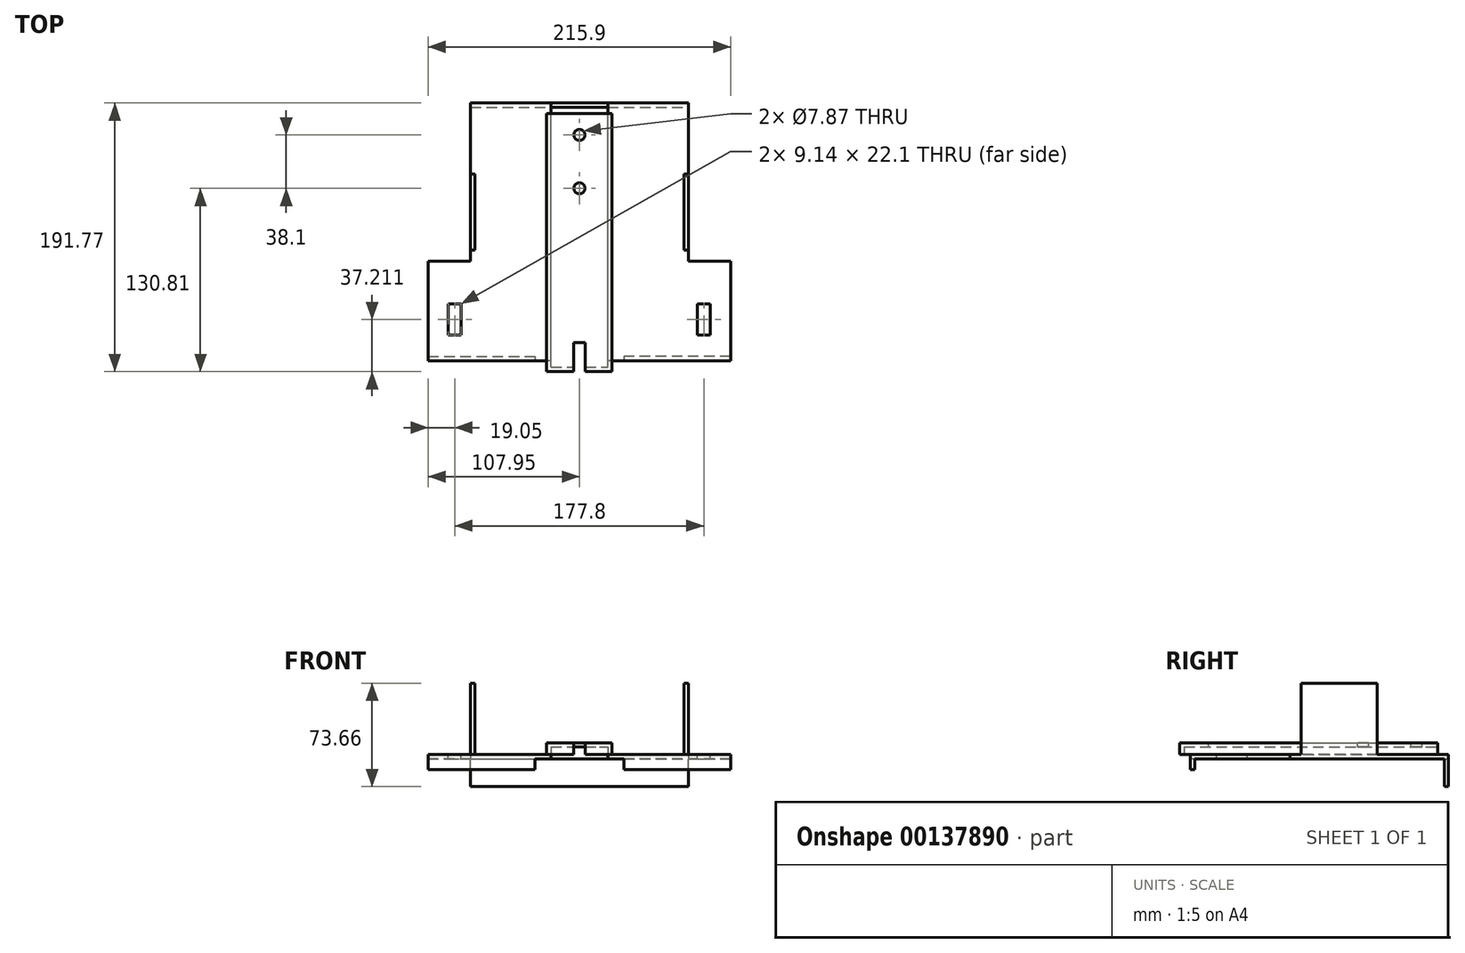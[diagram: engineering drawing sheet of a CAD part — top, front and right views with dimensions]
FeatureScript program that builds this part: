
annotation { "Feature Type Name" : "Feature", "Feature Type Description" : "" }
export const myFeature = defineFeature(function(context is Context, id is Id, definition is map)
    precondition{}
    {
        {
            var Q0;
            Q0=qCreatedBy(makeId("Top.planeOp"),FACE);
            var sketch = newSketch(context, id + "F0", { "sketchPlane" : qUnion([Q0])});
            skLineSegment(sketch, "E0.bottom", {"start": v(107.95, 0) * mm, "end": v(-107.95, 0) * mm});
            skLineSegment(sketch, "E0.top", {"start": v(77.79, 184.15) * mm, "end": v(-77.79, 184.15) * mm});
            skLineSegment(sketch, "E0.left", {"start": v(107.95, 0) * mm, "end": v(107.95, 71.12) * mm});
            skLineSegment(sketch, "E0.right", {"start": v(-107.95, 0) * mm, "end": v(-107.95, 71.12) * mm});
            skPoint(sketch, "E0.middle", {"position": v(0, 0) * mm});
            skLineSegment(sketch, "E1", {"start": v(-77.79, 184.15) * mm, "end": v(-77.79, 71.12) * mm});
            skLineSegment(sketch, "E2", {"start": v(-77.79, 71.12) * mm, "end": v(-107.95, 71.12) * mm});
            skLineSegment(sketch, "E3.MirrorCS", {"start": v(77.79, 184.15) * mm, "end": v(77.79, 71.12) * mm});
            skLineSegment(sketch, "E4.MirrorCS", {"start": v(77.79, 71.12) * mm, "end": v(107.95, 71.12) * mm});
            skLineSegment(sketch, "E5", {"start": v(0, 184.15) * mm, "end": v(0, 0) * mm, "construction": true});
            skSolve(sketch);
        }
        {
            var Q0;
            Q0 = qSketchRegion(id + "F0", true);
            extrude(context, id + "F1", {"entities" : qUnion([Q0]), "depth" : 3.1 * mm});
        }
        {
            var Q0;
            Q0=makeQuery(id+"F1.opExtrude","CAP_FACE",FACE,{"disambiguationData":[OSD([sQuery(id+"F0.wireOp",EDGE,"E0.bottom"),sQuery(id+"F0.wireOp",EDGE,"E0.top"),sQuery(id+"F0.wireOp",EDGE,"E0.left"),sQuery(id+"F0.wireOp",EDGE,"E0.right"),sQuery(id+"F0.wireOp",EDGE,"E1"),sQuery(id+"F0.wireOp",EDGE,"E2"),sQuery(id+"F0.wireOp",EDGE,"E3.MirrorCS"),sQuery(id+"F0.wireOp",EDGE,"E4.MirrorCS")])],"isStart":false});
            var sketch = newSketch(context, id + "F2", { "sketchPlane" : qUnion([Q0])});
            skLineSegment(sketch, "E6.bottom", {"start": v(107.95, 0) * mm, "end": v(31.75, 0) * mm});
            skLineSegment(sketch, "E6.top", {"start": v(107.95, 3.1) * mm, "end": v(31.75, 3.1) * mm});
            skLineSegment(sketch, "E6.left", {"start": v(107.95, 3.1) * mm, "end": v(107.95, 0) * mm});
            skLineSegment(sketch, "E6.right", {"start": v(31.75, 3.1) * mm, "end": v(31.75, 0) * mm});
            skLineSegment(sketch, "E7.MirrorCS", {"start": v(-31.75, 3.1) * mm, "end": v(-31.75, 0) * mm});
            skLineSegment(sketch, "E8.MirrorCS", {"start": v(-107.95, 3.1) * mm, "end": v(-107.95, 0) * mm});
            skLineSegment(sketch, "E9.MirrorCS", {"start": v(-107.95, 0) * mm, "end": v(-31.75, 0) * mm});
            skLineSegment(sketch, "E10.MirrorCS", {"start": v(-107.95, 3.1) * mm, "end": v(-31.75, 3.1) * mm});
            skSolve(sketch);
        }
        {
            var Q0;
            Q0 = qSketchRegion(id + "F2", true);
            extrude(context, id + "F3", {"entities" : qUnion([Q0]), "operationType" : NewBodyOperationType.ADD, "oppositeDirection" : true, "depth" : 10.92 * mm});
        }
        {
            var Q0;
            Q0=makeQuery(id+"F1.opExtrude","CAP_FACE",FACE,{"disambiguationData":[OSD([sQuery(id+"F0.wireOp",EDGE,"E0.bottom"),sQuery(id+"F0.wireOp",EDGE,"E0.top"),sQuery(id+"F0.wireOp",EDGE,"E0.left"),sQuery(id+"F0.wireOp",EDGE,"E0.right"),sQuery(id+"F0.wireOp",EDGE,"E1"),sQuery(id+"F0.wireOp",EDGE,"E2"),sQuery(id+"F0.wireOp",EDGE,"E3.MirrorCS"),sQuery(id+"F0.wireOp",EDGE,"E4.MirrorCS")])],"isStart":false});
            var sketch = newSketch(context, id + "F4", { "sketchPlane" : qUnion([Q0])});
            skLineSegment(sketch, "E11.bottom", {"start": v(-77.79, 184.15) * mm, "end": v(77.79, 184.15) * mm});
            skLineSegment(sketch, "E11.top", {"start": v(-77.79, 181.05) * mm, "end": v(77.79, 181.05) * mm});
            skLineSegment(sketch, "E11.left", {"start": v(-77.79, 184.15) * mm, "end": v(-77.79, 181.05) * mm});
            skLineSegment(sketch, "E11.right", {"start": v(77.79, 184.15) * mm, "end": v(77.79, 181.05) * mm});
            skSolve(sketch);
        }
        {
            var Q0;
            Q0 = qSketchRegion(id + "F4", true);
            extrude(context, id + "F5", {"entities" : qUnion([Q0]), "operationType" : NewBodyOperationType.ADD, "oppositeDirection" : true, "depth" : 22.86 * mm});
        }
        {
            var Q0;
            Q0=makeQuery(id+"F1.opExtrude","CAP_FACE",FACE,{"disambiguationData":[OSD([sQuery(id+"F0.wireOp",EDGE,"E0.bottom"),sQuery(id+"F0.wireOp",EDGE,"E0.top"),sQuery(id+"F0.wireOp",EDGE,"E0.left"),sQuery(id+"F0.wireOp",EDGE,"E0.right"),sQuery(id+"F0.wireOp",EDGE,"E1"),sQuery(id+"F0.wireOp",EDGE,"E2"),sQuery(id+"F0.wireOp",EDGE,"E3.MirrorCS"),sQuery(id+"F0.wireOp",EDGE,"E4.MirrorCS")])],"isStart":false});
            var sketch = newSketch(context, id + "F6", { "sketchPlane" : qUnion([Q0])});
            skLineSegment(sketch, "E12.bottom", {"start": v(-23.33, -7.62) * mm, "end": v(23.33, -7.62) * mm});
            skLineSegment(sketch, "E12.left", {"start": v(-23.33, -7.62) * mm, "end": v(-23.33, 176.53) * mm});
            skLineSegment(sketch, "E12.right", {"start": v(23.33, -7.62) * mm, "end": v(23.33, 176.53) * mm});
            skLineSegment(sketch, "E13", {"start": v(-23.33, 176.53) * mm, "end": v(23.33, 176.53) * mm});
            skSolve(sketch);
        }
        {
            var Q0;
            Q0 = qSketchRegion(id + "F6", true);
            extrude(context, id + "F7", {"entities" : qUnion([Q0]), "operationType" : NewBodyOperationType.ADD, "depth" : 8.33 * mm});
        }
        {
            var Q0;
            Q0=makeQuery(id+"F1.opExtrude","CAP_FACE",FACE,{"disambiguationData":[OSD([sQuery(id+"F0.wireOp",EDGE,"E0.bottom"),sQuery(id+"F0.wireOp",EDGE,"E0.top"),sQuery(id+"F0.wireOp",EDGE,"E0.left"),sQuery(id+"F0.wireOp",EDGE,"E0.right"),sQuery(id+"F0.wireOp",EDGE,"E1"),sQuery(id+"F0.wireOp",EDGE,"E2"),sQuery(id+"F0.wireOp",EDGE,"E3.MirrorCS"),sQuery(id+"F0.wireOp",EDGE,"E4.MirrorCS")])],"isStart":true});
            var sketch = newSketch(context, id + "F8", { "sketchPlane" : qUnion([Q0])});
            skLineSegment(sketch, "E14.bottom", {"start": v(-20.23, 15.8) * mm, "end": v(20.23, 15.8) * mm});
            skLineSegment(sketch, "E14.top", {"start": v(-20.23, -199.77) * mm, "end": v(20.23, -199.77) * mm});
            skLineSegment(sketch, "E14.left", {"start": v(-20.23, 15.8) * mm, "end": v(-20.23, -199.77) * mm});
            skLineSegment(sketch, "E14.right", {"start": v(20.23, 15.8) * mm, "end": v(20.23, -199.77) * mm});
            skSolve(sketch);
        }
        {
            var Q0;
            Q0 = qSketchRegion(id + "F8", true);
            extrude(context, id + "F9", {"entities" : qUnion([Q0]), "operationType" : NewBodyOperationType.REMOVE, "oppositeDirection" : true, "depth" : 3.1 * mm});
        }
        {
            var Q0;
            Q0=makeQuery(id+"F9.boolean.opBoolean","MERGE",FACE,{"derivedFrom":[makeQuery(id+"F7.opExtrude","CAP_FACE",FACE,{"disambiguationData":[OSD([sQuery(id+"F6.wireOp",EDGE,"E12.bottom"),sQuery(id+"F6.wireOp",EDGE,"E12.left"),sQuery(id+"F6.wireOp",EDGE,"E12.right"),sQuery(id+"F6.wireOp",EDGE,"E13")])],"isStart":true}),makeQuery(id+"F9.opExtrude","CAP_FACE",FACE,{"disambiguationData":[OSD([sQuery(id+"F8.wireOp",EDGE,"E14.bottom"),sQuery(id+"F8.wireOp",EDGE,"E14.top"),sQuery(id+"F8.wireOp",EDGE,"E14.left"),sQuery(id+"F8.wireOp",EDGE,"E14.right")])],"isStart":false})]});
            shell(context, id + "F10", {"entities" : qUnion([Q0]), "thickness" : 3.1 * mm});
        }
        {
            var Q0;
            Q0=makeQuery(id+"F10.opShell","OFFSET_FACE",FACE,{"disambiguationData":[OSD([sQuery(id+"F6.wireOp",EDGE,"E13")])]});
            extrude(context, id + "F11", {"entities" : qUnion([Q0]), "operationType" : NewBodyOperationType.REMOVE, "endBound" : BoundingType.UP_TO_NEXT, "oppositeDirection" : true, "depth" : 25.4 * mm});
        }
        {
            var Q0;
            Q0=makeQuery(id+"F7.opExtrude","CAP_FACE",FACE,{"disambiguationData":[OSD([sQuery(id+"F6.wireOp",EDGE,"E12.bottom"),sQuery(id+"F6.wireOp",EDGE,"E12.left"),sQuery(id+"F6.wireOp",EDGE,"E12.right"),sQuery(id+"F6.wireOp",EDGE,"E13")])],"isStart":false});
            var sketch = newSketch(context, id + "F12", { "sketchPlane" : qUnion([Q0])});
            skLineSegment(sketch, "E15.bottom", {"start": v(-4.23, -7.62) * mm, "end": v(4.23, -7.62) * mm});
            skLineSegment(sketch, "E15.top", {"start": v(-4.23, 12.95) * mm, "end": v(4.23, 12.95) * mm});
            skLineSegment(sketch, "E15.left", {"start": v(-4.23, -7.62) * mm, "end": v(-4.23, 12.95) * mm});
            skLineSegment(sketch, "E15.right", {"start": v(4.23, -7.62) * mm, "end": v(4.23, 12.95) * mm});
            skSolve(sketch);
        }
        {
            var Q0;
            Q0 = qSketchRegion(id + "F12", true);
            var Q1;
            Q1=makeQuery(id+"F9.boolean.opBoolean","MERGE",FACE,{"derivedFrom":[makeQuery(id+"F7.opExtrude","CAP_FACE",FACE,{"disambiguationData":[OSD([sQuery(id+"F6.wireOp",EDGE,"E12.bottom"),sQuery(id+"F6.wireOp",EDGE,"E12.left"),sQuery(id+"F6.wireOp",EDGE,"E12.right"),sQuery(id+"F6.wireOp",EDGE,"E13")])],"isStart":true}),makeQuery(id+"F9.opExtrude","CAP_FACE",FACE,{"disambiguationData":[OSD([sQuery(id+"F8.wireOp",EDGE,"E14.bottom"),sQuery(id+"F8.wireOp",EDGE,"E14.top"),sQuery(id+"F8.wireOp",EDGE,"E14.left"),sQuery(id+"F8.wireOp",EDGE,"E14.right")])],"isStart":false})]});
            extrude(context, id + "F13", {"entities" : qUnion([Q0]), "operationType" : NewBodyOperationType.REMOVE, "endBound" : BoundingType.UP_TO_SURFACE, "oppositeDirection" : true, "endBoundEntityFace" : qUnion([Q1]), "depth" : 25.4 * mm});
        }
        {
            var Q0;
            {var subQ0=sQuery(id+"F0.wireOp",EDGE,"E1");var subQ1=sQuery(id+"F0.wireOp",EDGE,"E2");var subQ2=sQuery(id+"F0.wireOp",EDGE,"E0.bottom");var subQ3=sQuery(id+"F0.wireOp",EDGE,"E0.top");var subQ4=sQuery(id+"F0.wireOp",EDGE,"E0.right");Q0=makeQuery(id+"F9.boolean.opBoolean","SPLIT",FACE,{"disambiguationData":[TD([makeQuery(id+"F1.opExtrude","SWEPT_FACE",FACE,{"disambiguationData":[OSD([subQ4])]})])],"derivedFrom":makeQuery(id+"F1.opExtrude","CAP_FACE",FACE,{"disambiguationData":[OSD([subQ2,subQ3,sQuery(id+"F0.wireOp",EDGE,"E0.left"),subQ4,subQ0,subQ1,sQuery(id+"F0.wireOp",EDGE,"E3.MirrorCS"),sQuery(id+"F0.wireOp",EDGE,"E4.MirrorCS")])],"isStart":false})});}
            var sketch = newSketch(context, id + "F14", { "sketchPlane" : qUnion([Q0])});
            skLineSegment(sketch, "E16.bottom", {"start": v(-77.79, 133.35) * mm, "end": v(-74.69, 133.35) * mm});
            skLineSegment(sketch, "E16.top", {"start": v(-77.79, 79) * mm, "end": v(-74.69, 79) * mm});
            skLineSegment(sketch, "E16.left", {"start": v(-77.79, 133.35) * mm, "end": v(-77.79, 79) * mm});
            skLineSegment(sketch, "E16.right", {"start": v(-74.69, 133.35) * mm, "end": v(-74.69, 79) * mm});
            skLineSegment(sketch, "E17.MirrorCS", {"start": v(74.69, 133.35) * mm, "end": v(74.69, 79) * mm});
            skLineSegment(sketch, "E18.MirrorCS", {"start": v(77.79, 133.35) * mm, "end": v(77.79, 79) * mm});
            skLineSegment(sketch, "E19.MirrorCS", {"start": v(77.79, 133.35) * mm, "end": v(74.69, 133.35) * mm});
            skLineSegment(sketch, "E20.MirrorCS", {"start": v(77.79, 79) * mm, "end": v(74.69, 79) * mm});
            skSolve(sketch);
        }
        {
            var Q0;
            Q0 = qSketchRegion(id + "F14", true);
            extrude(context, id + "F15", {"entities" : qUnion([Q0]), "operationType" : NewBodyOperationType.ADD, "depth" : 50.8 * mm});
        }
        {
            var Q0;
            {var subQ0=sQuery(id+"F0.wireOp",EDGE,"E4.MirrorCS");var subQ1=sQuery(id+"F0.wireOp",EDGE,"E0.bottom");var subQ2=sQuery(id+"F0.wireOp",EDGE,"E0.left");var subQ3=sQuery(id+"F0.wireOp",EDGE,"E0.top");var subQ4=sQuery(id+"F0.wireOp",EDGE,"E3.MirrorCS");Q0=makeQuery(id+"F9.boolean.opBoolean","SPLIT",FACE,{"disambiguationData":[TD([makeQuery(id+"F1.opExtrude","SWEPT_FACE",FACE,{"disambiguationData":[OSD([subQ2])]})])],"derivedFrom":makeQuery(id+"F1.opExtrude","CAP_FACE",FACE,{"disambiguationData":[OSD([subQ1,subQ3,subQ2,sQuery(id+"F0.wireOp",EDGE,"E0.right"),sQuery(id+"F0.wireOp",EDGE,"E1"),sQuery(id+"F0.wireOp",EDGE,"E2"),subQ4,subQ0])],"isStart":false})});}
            var sketch = newSketch(context, id + "F16", { "sketchPlane" : qUnion([Q0])});
            skLineSegment(sketch, "E21.bottom", {"start": v(93.47, 18.54) * mm, "end": v(84.33, 18.54) * mm});
            skLineSegment(sketch, "E21.top", {"start": v(93.47, 40.64) * mm, "end": v(84.33, 40.64) * mm});
            skLineSegment(sketch, "E21.left", {"start": v(93.47, 18.54) * mm, "end": v(93.47, 40.64) * mm});
            skLineSegment(sketch, "E21.right", {"start": v(84.33, 18.54) * mm, "end": v(84.33, 40.64) * mm});
            skLineSegment(sketch, "E22", {"start": v(88.9, 40.64) * mm, "end": v(88.9, 18.54) * mm, "construction": true});
            skArc(sketch, "E23", {"start": v(93.47, 36.07) * mm, "mid": v(88.9, 40.64) * mm, "end": v(84.33, 36.07) * mm, "construction": true});
            skArc(sketch, "E24", {"start": v(84.33, 23.11) * mm, "mid": v(88.9, 18.54) * mm, "end": v(93.47, 23.11) * mm, "construction": true});
            skArc(sketch, "E25.MirrorCS", {"start": v(93.47, 23.11) * mm, "mid": v(88.9, 18.54) * mm, "end": v(84.33, 23.11) * mm, "construction": true});
            skArc(sketch, "E26.MirrorCS", {"start": v(84.33, 36.07) * mm, "mid": v(88.9, 40.64) * mm, "end": v(93.47, 36.07) * mm, "construction": true});
            skLineSegment(sketch, "E27.MirrorCS", {"start": v(84.33, 18.54) * mm, "end": v(93.47, 18.54) * mm});
            skLineSegment(sketch, "E28.MirrorCS", {"start": v(84.33, 40.64) * mm, "end": v(93.47, 40.64) * mm});
            skLineSegment(sketch, "E29.MirrorCS", {"start": v(-84.33, 18.54) * mm, "end": v(-84.33, 40.64) * mm});
            skLineSegment(sketch, "E30.MirrorCS", {"start": v(-84.33, 18.54) * mm, "end": v(-93.47, 18.54) * mm});
            skLineSegment(sketch, "E31.MirrorCS", {"start": v(-84.33, 40.64) * mm, "end": v(-93.47, 40.64) * mm});
            skLineSegment(sketch, "E32.MirrorCS", {"start": v(-93.47, 18.54) * mm, "end": v(-93.47, 40.64) * mm});
            skArc(sketch, "E33.MirrorCS", {"start": v(-84.33, 36.07) * mm, "mid": v(-88.9, 40.64) * mm, "end": v(-93.47, 36.07) * mm, "construction": true});
            skArc(sketch, "E34.MirrorCS", {"start": v(-93.47, 23.11) * mm, "mid": v(-88.9, 18.54) * mm, "end": v(-84.33, 23.11) * mm, "construction": true});
            skLineSegment(sketch, "E35.MirrorCS", {"start": v(-93.47, 40.64) * mm, "end": v(-84.33, 40.64) * mm});
            skLineSegment(sketch, "E36.MirrorCS", {"start": v(-93.47, 18.54) * mm, "end": v(-84.33, 18.54) * mm});
            skLineSegment(sketch, "E37.MirrorCS", {"start": v(-88.9, 40.64) * mm, "end": v(-88.9, 18.54) * mm, "construction": true});
            skArc(sketch, "E38.MirrorCS", {"start": v(-84.33, 23.11) * mm, "mid": v(-88.9, 18.54) * mm, "end": v(-93.47, 23.11) * mm, "construction": true});
            skArc(sketch, "E39.MirrorCS", {"start": v(-93.47, 36.07) * mm, "mid": v(-88.9, 40.64) * mm, "end": v(-84.33, 36.07) * mm, "construction": true});
            skSolve(sketch);
        }
        {
            var Q0;
            Q0 = qSketchRegion(id + "F16", true);
            extrude(context, id + "F17", {"entities" : qUnion([Q0]), "operationType" : NewBodyOperationType.REMOVE, "endBound" : BoundingType.UP_TO_NEXT, "oppositeDirection" : true, "depth" : 25.4 * mm});
        }
        {
            var Q0;
            Q0=makeQuery(id+"F7.opExtrude","CAP_FACE",FACE,{"disambiguationData":[OSD([sQuery(id+"F6.wireOp",EDGE,"E12.bottom"),sQuery(id+"F6.wireOp",EDGE,"E12.left"),sQuery(id+"F6.wireOp",EDGE,"E12.right"),sQuery(id+"F6.wireOp",EDGE,"E13")])],"isStart":false});
            var sketch = newSketch(context, id + "F18", { "sketchPlane" : qUnion([Q0])});
            skCircle(sketch, "E40", {"center": v(0, 123.2) * mm, "radius": 3.94 * mm});
            skCircle(sketch, "E41", {"center": v(0, 161.3) * mm, "radius": 3.94 * mm});
            skSolve(sketch);
        }
        {
            var Q0;
            Q0 = qSketchRegion(id + "F18", true);
            extrude(context, id + "F19", {"entities" : qUnion([Q0]), "operationType" : NewBodyOperationType.REMOVE, "endBound" : BoundingType.UP_TO_NEXT, "oppositeDirection" : true, "depth" : 25.4 * mm});
        }
    });
